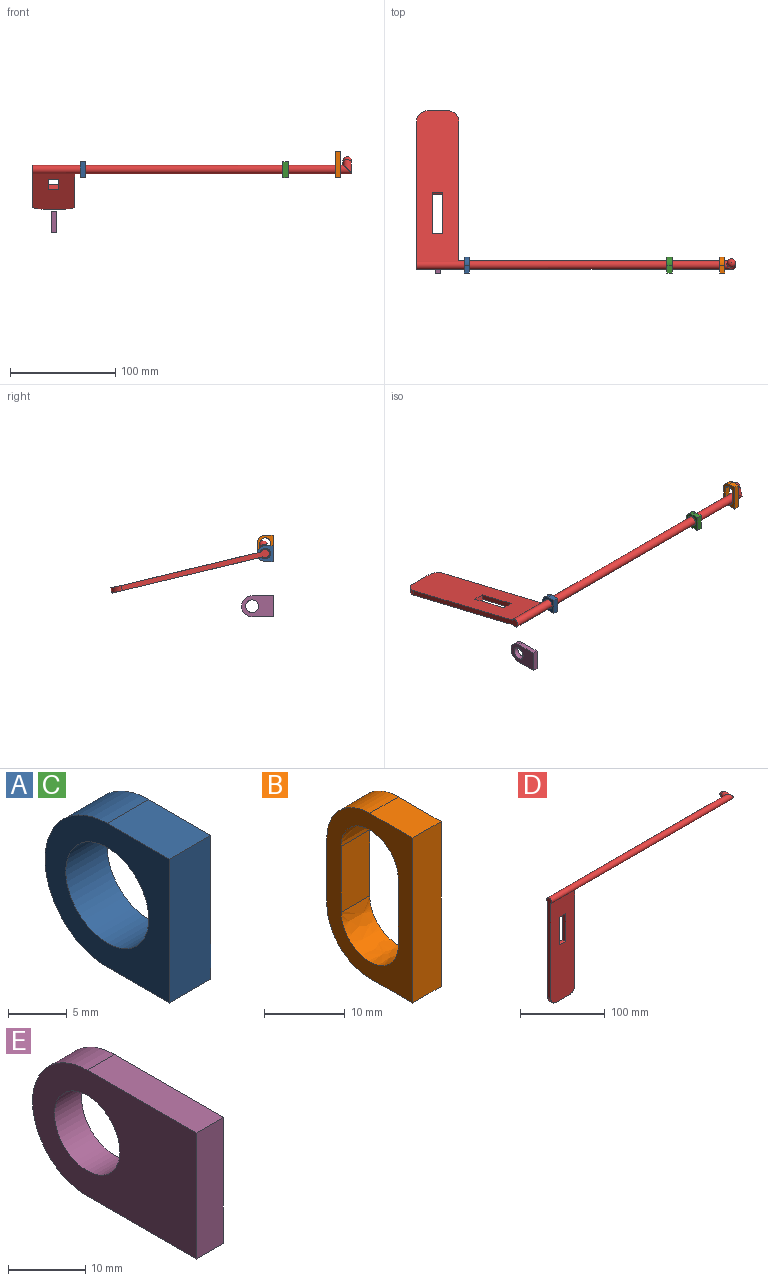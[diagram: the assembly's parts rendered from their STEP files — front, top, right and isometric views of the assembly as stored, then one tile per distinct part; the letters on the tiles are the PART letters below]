
ASSEMBLY  parts=5 mates=4
PART A: 7 faces, bbox 5x15x15 mm
  f0: plane 15x5mm, normal (0,-1,0), area 75mm2, adj f1,f3,f5,f6
  f1: plane 7.5x5mm, normal (0,0,-1), area 37.5mm2, adj f0,f2,f5,f6
  f2: cylinder r=7.5mm len=15mm, axis (-1,0,0), area 117.8mm2, adj f1,f3,f5,f6
  f3: plane 7.5x5mm, normal (0,0,1), area 37.5mm2, adj f0,f2,f5,f6
  f4: cylinder r=5mm len=10mm, axis (-1,0,0), area 157.1mm2, adj f5,f6
  f5: plane 15x15mm, normal (1,0,0), area 122.3mm2, adj f0,f1,f2,f3,f4
  f6: plane 15x15mm, normal (-1,0,0), area 122.3mm2, adj f0,f1,f2,f3,f4
PART B: 12 faces, bbox 5x15x25 mm
  f0: plane 25x5mm, normal (0,-1,0), area 125mm2, adj f1,f9,f10,f11
  f1: plane 7.5x5mm, normal (0,0,-1), area 37.5mm2, adj f0,f2,f10,f11
  f2: cylinder r=7.5mm len=7.5mm, axis (-1,0,0), area 58.9mm2, adj f1,f3,f10,f11
  f3: plane 10x5mm, normal (0,1,0), area 50mm2, adj f2,f4,f10,f11
  f4: cylinder r=7.5mm len=7.5mm, axis (-1,0,0), area 58.9mm2, adj f3,f9,f10,f11
  f5: plane 10x5mm, normal (0,1,0), area 50mm2, adj f6,f8,f10,f11
  f6: extruded ~10x5mm, area 78.5mm2, adj f5,f7,f10,f11
  f7: plane 10x5mm, normal (0,-1,0), area 50mm2, adj f6,f8,f10,f11
  f8: extruded ~10x5mm, area 78.5mm2, adj f5,f7,f10,f11
  f9: plane 7.5x5mm, normal (0,0,1), area 37.5mm2, adj f0,f4,f10,f11
  f10: plane 25x15mm, normal (1,0,0), area 172.3mm2, adj f0,f1,f2,f3,f4,f5,f6,f7
  f11: plane 25x15mm, normal (-1,0,0), area 172.3mm2, adj f0,f1,f2,f3,f4,f5,f6,f7
PART C: same geometry as A
PART D: 14 faces, bbox 302.5x16.5x154 mm
  f0: cylinder r=4mm len=302.52mm, axis (-1,0,0), area 7289.5mm2, adj f4,f8,f10,f11,f12
  f1: plane 10x5mm, normal (0,0,-1), area 50mm2, adj f2,f9,f10,f11
  f2: plane 40x5mm, normal (-1,0,0), area 200mm2, adj f1,f3,f10,f11
  f3: plane 10x5mm, normal (0,0,1), area 50mm2, adj f2,f9,f10,f11
  f4: plane 144x8mm, normal (-1,0,0), area 731.7mm2, adj f0,f5,f10,f11
  f5: cylinder r=10mm len=10mm, axis (0,1,0), area 78.5mm2, adj f4,f6,f10,f11
  f6: plane 20x5mm, normal (0,0,-1), area 100mm2, adj f5,f7,f10,f11
  f7: cylinder r=10mm len=10mm, axis (0,1,0), area 78.5mm2, adj f6,f8,f10,f11
  f8: plane 136.88x5mm, normal (1,0,0), area 681.4mm2, adj f0,f7,f10,f11
  f9: plane 40x5mm, normal (1,0,0), area 200mm2, adj f1,f3,f10,f11
  f10: plane 146.88x40mm, normal (0,-1,0), area 5432.2mm2, adj f0,f1,f2,f3,f4,f5,f6,f7
  f11: plane 146.88x40mm, normal (0,1,0), area 5432.2mm2, adj f0,f1,f2,f3,f4,f5,f6,f7
  f12: cylinder r=4mm len=12.52mm, axis (0,-1,0), area 217.1mm2, adj f0,f13
  f13: sphere r=4mm, area 100.5mm2, adj f12
PART E: 7 faces, bbox 5x30x20 mm
  f0: plane 20x5mm, normal (0,-1,0), area 100mm2, adj f1,f3,f5,f6
  f1: plane 20x5mm, normal (0,0,-1), area 100mm2, adj f0,f2,f5,f6
  f2: cylinder r=10mm len=20mm, axis (-1,0,0), area 157.1mm2, adj f1,f3,f5,f6
  f3: plane 20x5mm, normal (0,0,1), area 100mm2, adj f0,f2,f5,f6
  f4: cylinder r=6mm len=12mm, axis (-1,0,0), area 188.5mm2, adj f5,f6
  f5: plane 30x20mm, normal (1,0,0), area 444mm2, adj f0,f1,f2,f3,f4
  f6: plane 30x20mm, normal (-1,0,0), area 444mm2, adj f0,f1,f2,f3,f4
PLACE A t=(-135.49,39.02,-0.08)mm fixed
PLACE B t=(107.01,39.02,-0.08)mm
PLACE C t=(57.01,39.02,-0.08)mm
PLACE D rot(axis=(1,0,0),76.5deg) t=(-160.49,192.38,-27.6)mm
PLACE E t=(-162.99,39.02,-52.58)mm
MATE fastened B.f0 <-> C.f0  axis (0,-1,0) through (109.51,39.02,-0.08)mm
MATE fastened E.f0 <-> A.f0  axis (0,-1,0) through (-157.99,39.02,-42.58)mm
MATE cylindrical A.f2 <-> D.f0  axis (1,0,0) through (-130.49,46.52,7.42)mm
MATE fastened A.f0 <-> C.f0  axis (0,-1,0) through (-130.49,39.02,7.42)mm
